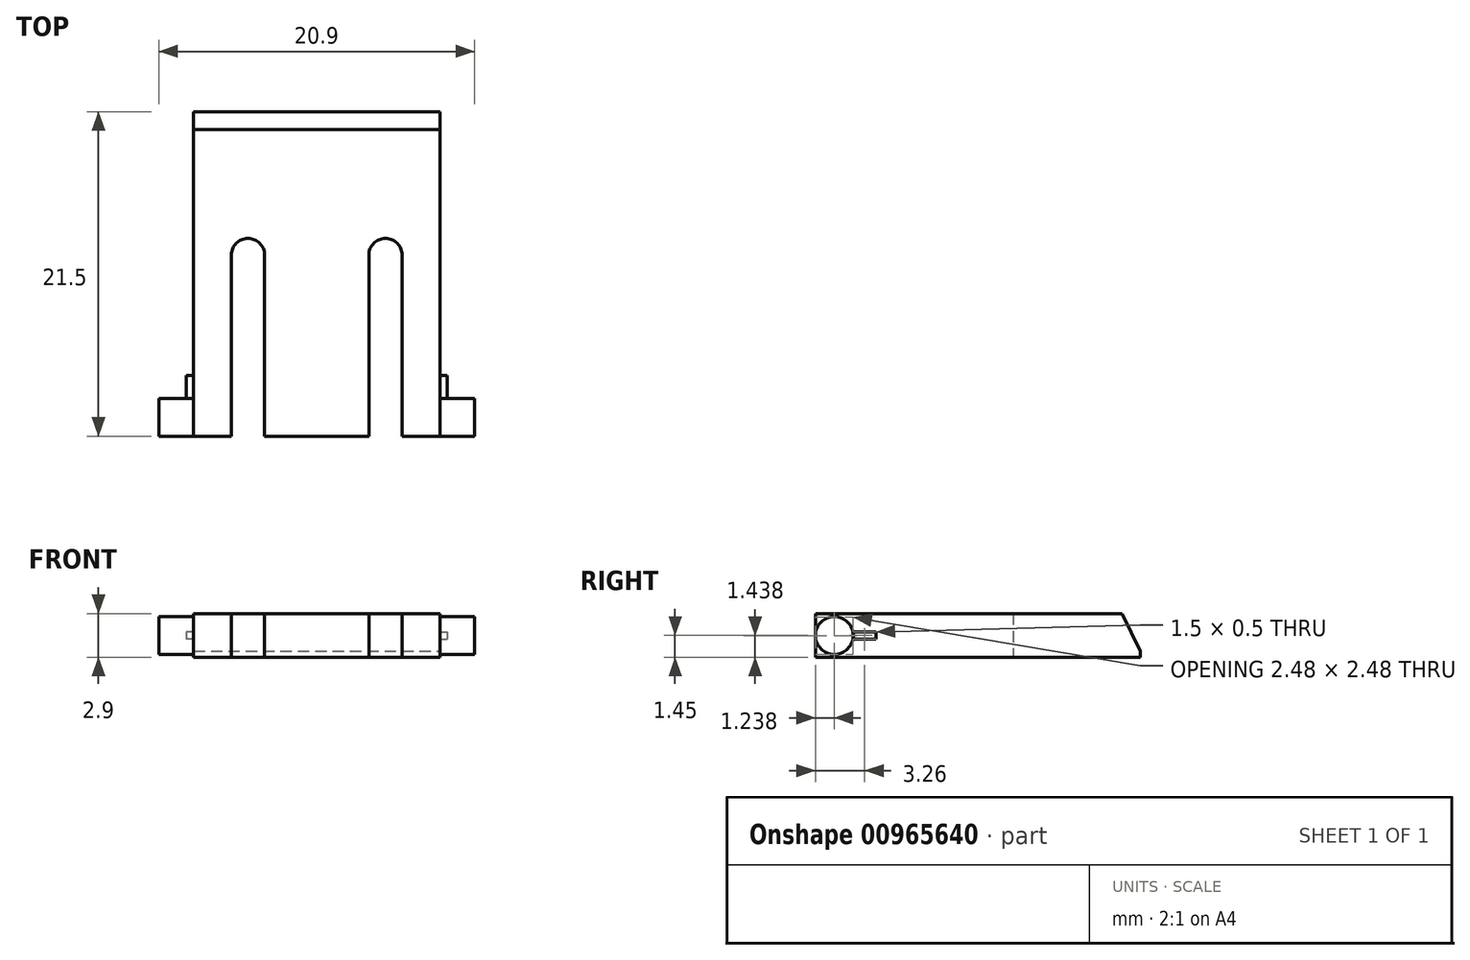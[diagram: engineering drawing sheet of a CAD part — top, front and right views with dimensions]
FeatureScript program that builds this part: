
annotation { "Feature Type Name" : "Feature", "Feature Type Description" : "" }
export const myFeature = defineFeature(function(context is Context, id is Id, definition is map)
    precondition{}
    {
        {
            var Q0;
            Q0=qCreatedBy(makeId("Top.planeOp"),FACE);
            var sketch = newSketch(context, id + "F0", { "sketchPlane" : qUnion([Q0])});
            skLineSegment(sketch, "E0.bottom", {"start": v(8.15, 10.75) * mm, "end": v(-8.15, 10.75) * mm});
            skLineSegment(sketch, "E0.top", {"start": v(8.15, -10.75) * mm, "end": v(5.65, -10.75) * mm});
            skLineSegment(sketch, "E0.left", {"start": v(8.15, 10.75) * mm, "end": v(8.15, -10.75) * mm});
            skLineSegment(sketch, "E0.right", {"start": v(-8.15, 10.75) * mm, "end": v(-8.15, -10.75) * mm});
            skPoint(sketch, "E0.middle", {"position": v(0, 0) * mm});
            skLineSegment(sketch, "E1.bottom", {"start": v(8.15, -10.75) * mm, "end": v(10.45, -10.75) * mm});
            skLineSegment(sketch, "E1.top", {"start": v(8.15, -8.25) * mm, "end": v(10.45, -8.25) * mm});
            skLineSegment(sketch, "E1.left", {"start": v(8.15, -10.75) * mm, "end": v(8.15, -8.25) * mm});
            skLineSegment(sketch, "E1.right", {"start": v(10.45, -10.75) * mm, "end": v(10.45, -8.25) * mm});
            skLineSegment(sketch, "E2.left", {"start": v(3.45, -10.75) * mm, "end": v(3.45, 1.25) * mm});
            skLineSegment(sketch, "E2.right", {"start": v(5.65, -10.75) * mm, "end": v(5.65, 1.25) * mm});
            skArc(sketch, "E3", {"start": v(5.65, 1.25) * mm, "mid": v(4.55, 2.35) * mm, "end": v(3.45, 1.25) * mm});
            skLineSegment(sketch, "E4.MirrorCS", {"start": v(-3.45, -10.75) * mm, "end": v(-3.45, 1.25) * mm});
            skArc(sketch, "E5.MirrorCS", {"start": v(-5.65, 1.25) * mm, "mid": v(-4.55, 2.35) * mm, "end": v(-3.45, 1.25) * mm});
            skLineSegment(sketch, "E6.MirrorCS", {"start": v(-5.65, -10.75) * mm, "end": v(-5.65, 1.25) * mm});
            skLineSegment(sketch, "E7.MirrorCS", {"start": v(-8.15, -8.25) * mm, "end": v(-10.45, -8.25) * mm});
            skLineSegment(sketch, "E8.MirrorCS", {"start": v(-8.15, -10.75) * mm, "end": v(-10.45, -10.75) * mm});
            skLineSegment(sketch, "E9.MirrorCS", {"start": v(-10.45, -10.75) * mm, "end": v(-10.45, -8.25) * mm});
            skPoint(sketch, "E10.MirrorCS.start.orphan", {"position": v(-3.45, -10.75) * mm});
            skLineSegment(sketch, "E11.trimOffspring", {"start": v(-5.65, -10.75) * mm, "end": v(-8.15, -10.75) * mm});
            skLineSegment(sketch, "E12.trimOffspring", {"start": v(3.45, -10.75) * mm, "end": v(-3.45, -10.75) * mm});
            skLineSegment(sketch, "E13", {"start": v(8.15, -9.5) * mm, "end": v(10.45, -9.5) * mm});
            skPoint(sketch, "E14.MirrorP", {"position": v(0, -19) * mm});
            skLineSegment(sketch, "E15.MirrorCS", {"start": v(-8.15, -9.5) * mm, "end": v(-10.45, -9.5) * mm});
            skLineSegment(sketch, "E16.bottom", {"start": v(8.15, -6.74) * mm, "end": v(8.65, -6.74) * mm});
            skLineSegment(sketch, "E16.top", {"start": v(8.15, -8.24) * mm, "end": v(8.65, -8.24) * mm});
            skLineSegment(sketch, "E16.left", {"start": v(8.15, -6.74) * mm, "end": v(8.15, -8.24) * mm});
            skLineSegment(sketch, "E16.right", {"start": v(8.65, -6.74) * mm, "end": v(8.65, -8.24) * mm});
            skLineSegment(sketch, "E17.MirrorCS", {"start": v(-8.15, -8.24) * mm, "end": v(-8.65, -8.24) * mm});
            skLineSegment(sketch, "E18.MirrorCS", {"start": v(-8.65, -6.74) * mm, "end": v(-8.65, -8.24) * mm});
            skLineSegment(sketch, "E19.MirrorCS", {"start": v(-8.15, -6.74) * mm, "end": v(-8.15, -8.24) * mm});
            skLineSegment(sketch, "E20.MirrorCS", {"start": v(-8.15, -6.74) * mm, "end": v(-8.65, -6.74) * mm});
            skSolve(sketch);
        }
        {
            var Q0;
            {var subQ3=sQuery(id+"F0.wireOp",EDGE,"E0.bottom");Q0=makeQuery(id+"F0.imprint","IMPRINT",FACE,{"disambiguationData":[TD([[makeQuery(id+"F0.imprint","IMPRINT",EDGE,{"derivedFrom":subQ3}),1.0]])]});}
            extrude(context, id + "F1", {"entities" : qUnion([Q0]), "endBound" : BoundingType.SYMMETRIC, "depth" : 2.9 * mm, "offsetDistance" : 25 * mm});
        }
        {
            var Q0;
            {var subQ0=sQuery(id+"F0.wireOp",EDGE,"E1.bottom");Q0=makeQuery(id+"F0.imprint","IMPRINT",FACE,{"disambiguationData":[TD([[makeQuery(id+"F0.imprint","IMPRINT",EDGE,{"derivedFrom":subQ0}),1.0]])]});}
            var Q1;
            Q1=sQuery(id+"F0.wireOp",EDGE,"E13");
            revolve(context, id + "F2", {"operationType" : NewBodyOperationType.ADD, "surfaceOperationType" : NewSurfaceOperationType.NEW, "entities" : qUnion([Q0]), "axis" : qUnion([Q1]), "revolveType" : RevolveType.FULL});
        }
        {
            var Q0;
            {var subQ0=sQuery(id+"F0.wireOp",EDGE,"E8.MirrorCS");Q0=makeQuery(id+"F0.imprint","IMPRINT",FACE,{"disambiguationData":[TD([[makeQuery(id+"F0.imprint","IMPRINT",EDGE,{"derivedFrom":subQ0}),-1.0]])]});}
            var Q1;
            Q1=sQuery(id+"F0.wireOp",EDGE,"E15.MirrorCS");
            revolve(context, id + "F3", {"operationType" : NewBodyOperationType.ADD, "surfaceOperationType" : NewSurfaceOperationType.NEW, "entities" : qUnion([Q0]), "axis" : qUnion([Q1]), "revolveType" : RevolveType.FULL});
        }
        {
            var Q0;
            Q0=makeQuery(id+"F1.opExtrude","CAP_EDGE",EDGE,{"disambiguationData":[OSD([sQuery(id+"F0.wireOp",EDGE,"E0.bottom")])],"isStart":false});
            chamfer(context, id + "F4", {"entities" : qUnion([Q0]), "chamferType" : ChamferType.TWO_OFFSETS, "width1" : 2.5 * mm, "oppositeDirection" : true, "width2" : 1.2 * mm, "tangentPropagation" : true});
        }
        {
            var Q0;
            Q0=makeQuery(id+"F0.imprint","IMPRINT",FACE,{"disambiguationData":[TD([[makeQuery(id+"F0.imprint","IMPRINT",EDGE,{"derivedFrom":sQuery(id+"F0.wireOp",EDGE,"E16.bottom")}),-1.0]])]});
            extrude(context, id + "F5", {"entities" : qUnion([Q0]), "operationType" : NewBodyOperationType.ADD, "endBound" : BoundingType.SYMMETRIC, "depth" : 0.5 * mm, "offsetDistance" : 25 * mm});
        }
        {
            var Q0;
            Q0=makeQuery(id+"F0.imprint","IMPRINT",FACE,{"disambiguationData":[TD([[makeQuery(id+"F0.imprint","IMPRINT",EDGE,{"derivedFrom":sQuery(id+"F0.wireOp",EDGE,"E17.MirrorCS")}),-1.0]])]});
            extrude(context, id + "F6", {"entities" : qUnion([Q0]), "operationType" : NewBodyOperationType.ADD, "endBound" : BoundingType.SYMMETRIC, "depth" : 0.5 * mm, "offsetDistance" : 25 * mm});
        }
    });
